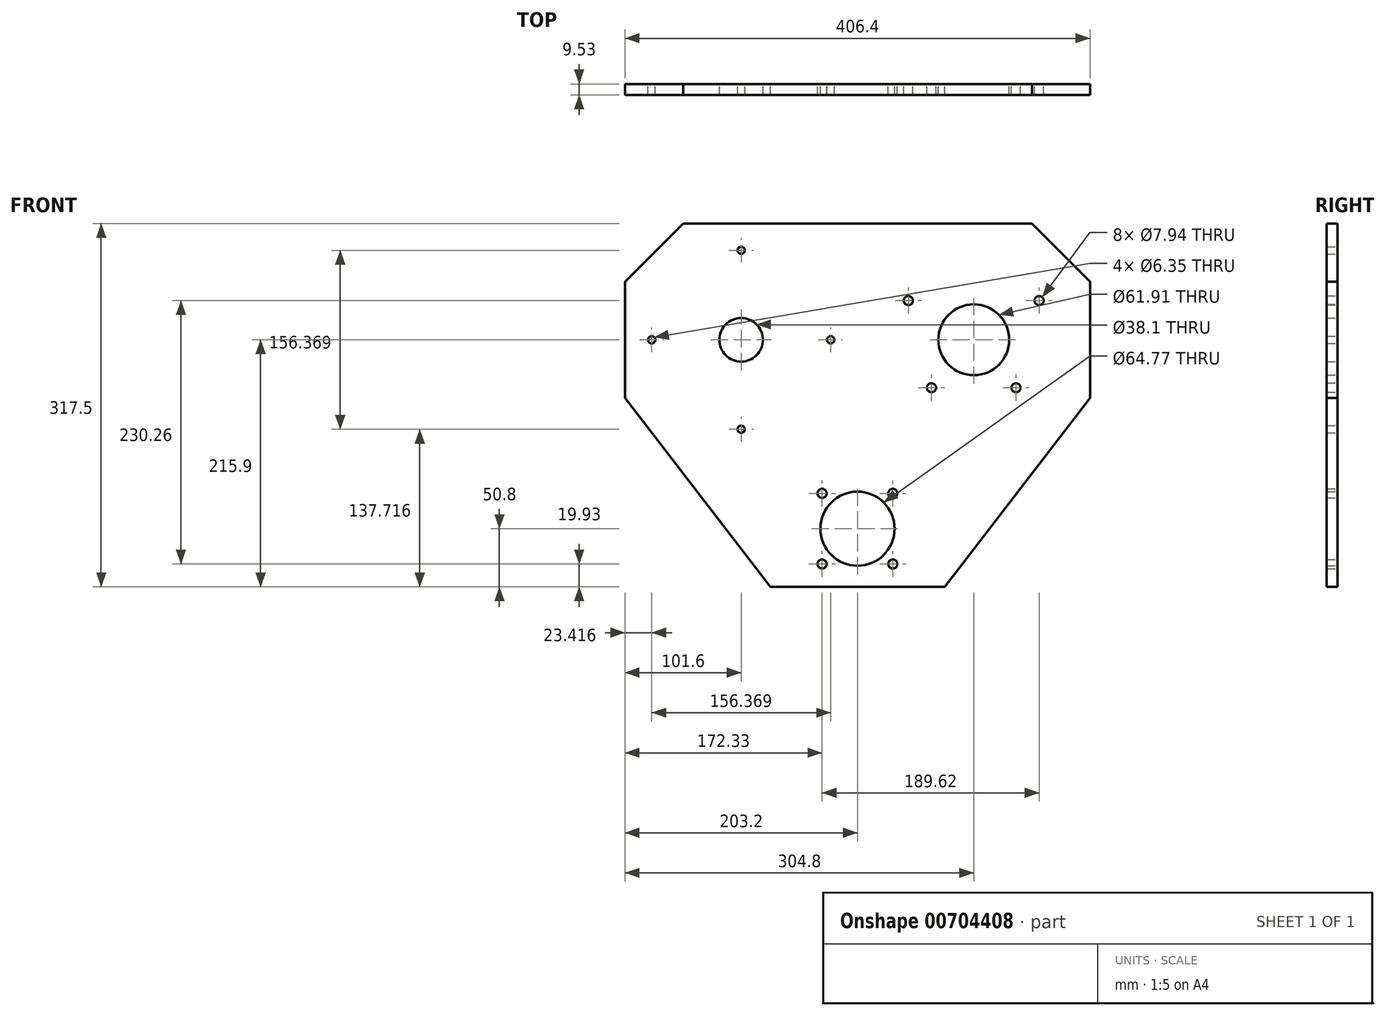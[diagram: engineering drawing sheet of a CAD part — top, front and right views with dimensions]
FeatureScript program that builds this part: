
annotation { "Feature Type Name" : "Feature", "Feature Type Description" : "" }
export const myFeature = defineFeature(function(context is Context, id is Id, definition is map)
    precondition{}
    {
        {
            var Q0;
            Q0=qCreatedBy(makeId("Front.planeOp"),FACE);
            var sketch = newSketch(context, id + "F0", { "sketchPlane" : qUnion([Q0])});
            skLineSegment(sketch, "E0", {"start": v(0, 0) * mm, "end": v(76.2, 0) * mm});
            skLineSegment(sketch, "E1", {"start": v(76.2, 0) * mm, "end": v(203.2, 165.1) * mm});
            skLineSegment(sketch, "E2", {"start": v(203.2, 165.1) * mm, "end": v(203.2, 266.7) * mm});
            skLineSegment(sketch, "E3", {"start": v(203.2, 266.7) * mm, "end": v(152.4, 317.5) * mm});
            skLineSegment(sketch, "E4", {"start": v(152.4, 317.5) * mm, "end": v(0, 317.5) * mm});
            skLineSegment(sketch, "E5", {"start": v(0, 317.5) * mm, "end": v(0, 0) * mm, "construction": true});
            skLineSegment(sketch, "E6.MirrorCS", {"start": v(-152.4, 317.5) * mm, "end": v(0, 317.5) * mm});
            skLineSegment(sketch, "E7.MirrorCS", {"start": v(-203.2, 266.7) * mm, "end": v(-152.4, 317.5) * mm});
            skLineSegment(sketch, "E8.MirrorCS", {"start": v(-203.2, 165.1) * mm, "end": v(-203.2, 266.7) * mm});
            skLineSegment(sketch, "E9.MirrorCS", {"start": v(-76.2, 0) * mm, "end": v(-203.2, 165.1) * mm});
            skLineSegment(sketch, "E10.MirrorCS", {"start": v(0, 0) * mm, "end": v(-76.2, 0) * mm});
            skLineSegment(sketch, "E11", {"start": v(-90.13, 50.8) * mm, "end": v(81.3, 50.8) * mm, "construction": true});
            skCircle(sketch, "E12", {"center": v(101.6, 215.9) * mm, "radius": 30.96 * mm});
            skCircle(sketch, "E13", {"center": v(-101.6, 215.9) * mm, "radius": 19.05 * mm});
            skLineSegment(sketch, "E14", {"start": v(-203.2, 215.9) * mm, "end": v(0, 215.9) * mm, "construction": true});
            skLineSegment(sketch, "E15", {"start": v(0, 215.9) * mm, "end": v(203.2, 215.9) * mm, "construction": true});
            skLineSegment(sketch, "E16", {"start": v(101.6, 215.9) * mm, "end": v(101.6, 259.6) * mm, "construction": true});
            skCircle(sketch, "E17", {"center": v(64.7, 174) * mm, "radius": 3.97 * mm});
            skCircle(sketch, "E18", {"center": v(44.45, 250.19) * mm, "radius": 3.97 * mm});
            skCircle(sketch, "E19.MirrorC", {"center": v(158.75, 250.2) * mm, "radius": 3.97 * mm});
            skCircle(sketch, "E20.MirrorC", {"center": v(138.5, 174) * mm, "radius": 3.97 * mm});
            skCircle(sketch, "E21", {"center": v(0, 50.8) * mm, "radius": 32.39 * mm});
            skLineSegment(sketch, "E22", {"start": v(-101.6, 215.9) * mm, "end": v(-101.6, 294.08) * mm, "construction": true});
            skCircle(sketch, "E23", {"center": v(-101.6, 294.08) * mm, "radius": 3.18 * mm});
            skCircle(sketch, "E24", {"center": v(-179.78, 215.9) * mm, "radius": 3.18 * mm});
            skCircle(sketch, "E25.MirrorC", {"center": v(-23.42, 215.9) * mm, "radius": 3.18 * mm});
            skCircle(sketch, "E26.MirrorC", {"center": v(-101.6, 137.72) * mm, "radius": 3.18 * mm});
            skLineSegment(sketch, "E27", {"start": v(0, 50.8) * mm, "end": v(-30.87, 81.67) * mm, "construction": true});
            skLineSegment(sketch, "E28", {"start": v(0, 50.8) * mm, "end": v(30.87, 81.67) * mm, "construction": true});
            skCircle(sketch, "E29", {"center": v(-30.87, 81.67) * mm, "radius": 3.97 * mm});
            skCircle(sketch, "E30", {"center": v(30.87, 81.67) * mm, "radius": 3.97 * mm});
            skCircle(sketch, "E31.MirrorC", {"center": v(-30.87, 19.93) * mm, "radius": 3.97 * mm});
            skCircle(sketch, "E32.MirrorC", {"center": v(30.87, 19.93) * mm, "radius": 3.97 * mm});
            skLineSegment(sketch, "E33", {"start": v(44.45, 174) * mm, "end": v(64.7, 174) * mm, "construction": true});
            skLineSegment(sketch, "E34", {"start": v(44.45, 250.19) * mm, "end": v(44.45, 215.9) * mm, "construction": true});
            skLineSegment(sketch, "E35", {"start": v(44.45, 174) * mm, "end": v(44.45, 215.9) * mm, "construction": true});
            skLineSegment(sketch, "E36", {"start": v(101.6, 174) * mm, "end": v(101.6, 215.9) * mm, "construction": true});
            skLineSegment(sketch, "E37", {"start": v(64.7, 174) * mm, "end": v(101.6, 174) * mm, "construction": true});
            skLineSegment(sketch, "E38", {"start": v(101.6, 174) * mm, "end": v(138.5, 174) * mm, "construction": true});
            skSolve(sketch);
        }
        {
            var Q0;
            Q0 = qSketchRegion(id + "F0", true);
            extrude(context, id + "F1", {"entities" : qUnion([Q0]), "depth" : 9.52 * mm, "offsetDistance" : 25.4 * mm});
        }
    });
